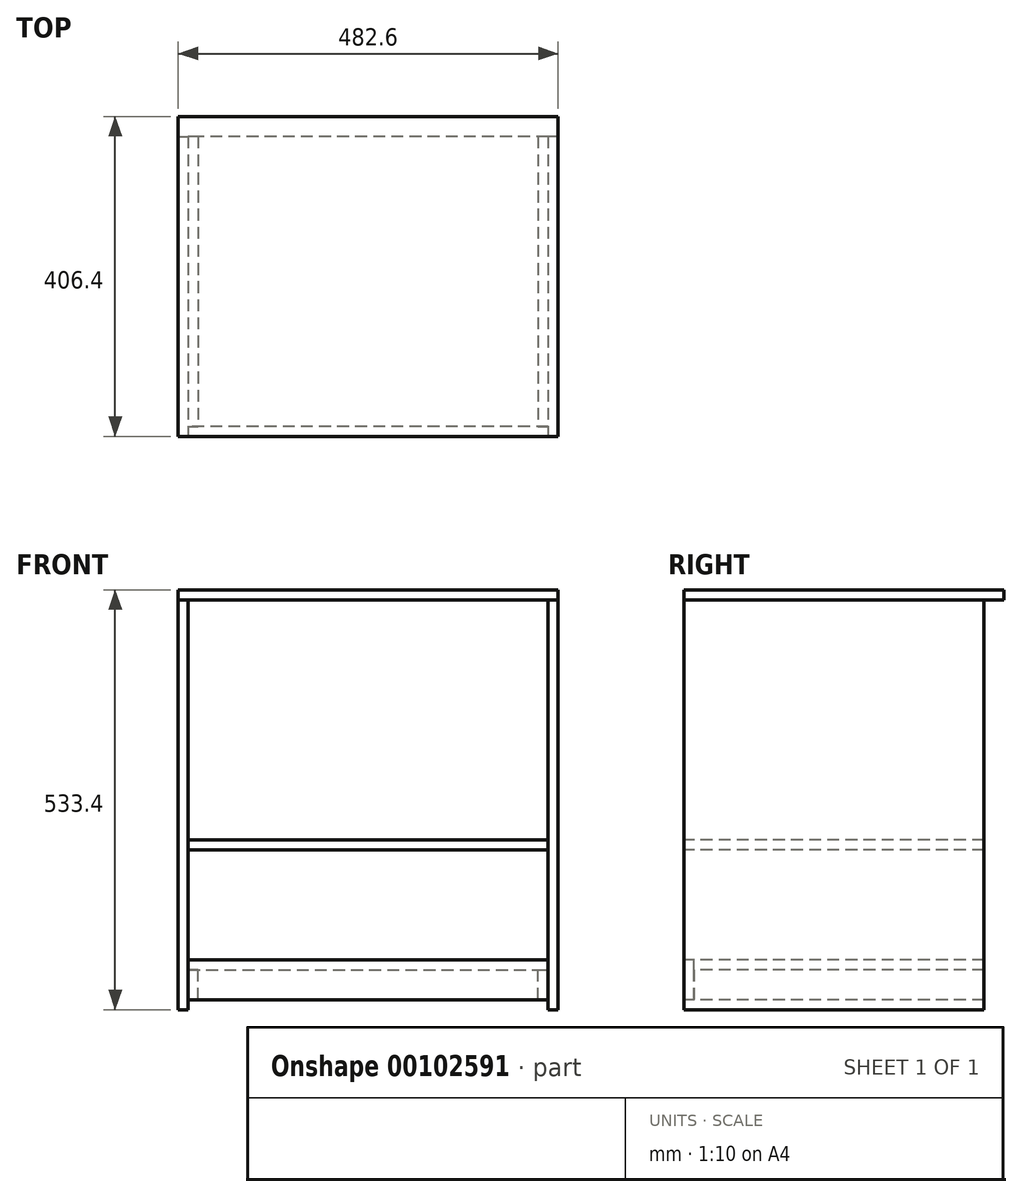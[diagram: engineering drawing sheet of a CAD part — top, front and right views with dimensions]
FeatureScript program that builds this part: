
annotation { "Feature Type Name" : "Feature", "Feature Type Description" : "" }
export const myFeature = defineFeature(function(context is Context, id is Id, definition is map)
    precondition{}
    {
        {
            var Q0;
            Q0=qCreatedBy(makeId("Front.planeOp"),FACE);
            var sketch = newSketch(context, id + "F0", { "sketchPlane" : qUnion([Q0])});
            skLineSegment(sketch, "E0.bottom", {"start": v(-241.3, 6.35) * mm, "end": v(241.3, 6.35) * mm});
            skLineSegment(sketch, "E0.top", {"start": v(-241.3, -6.35) * mm, "end": v(241.3, -6.35) * mm});
            skLineSegment(sketch, "E0.left", {"start": v(-241.3, 6.35) * mm, "end": v(-241.3, -6.35) * mm});
            skLineSegment(sketch, "E0.right", {"start": v(241.3, 6.35) * mm, "end": v(241.3, -6.35) * mm});
            skPoint(sketch, "E0.middle", {"position": v(0, 0) * mm});
            skLineSegment(sketch, "E1", {"start": v(0, 0) * mm, "end": v(0, -514.35) * mm, "construction": true});
            skLineSegment(sketch, "E2", {"start": v(-241.3, -6.35) * mm, "end": v(-241.3, -527.05) * mm});
            skLineSegment(sketch, "E3", {"start": v(-241.3, -527.05) * mm, "end": v(-228.6, -527.05) * mm});
            skLineSegment(sketch, "E4", {"start": v(-228.6, -527.05) * mm, "end": v(-228.6, -6.35) * mm});
            skLineSegment(sketch, "E5", {"start": v(-228.6, -476.25) * mm, "end": v(-215.9, -476.25) * mm});
            skLineSegment(sketch, "E6", {"start": v(-215.9, -476.25) * mm, "end": v(-215.9, -514.35) * mm});
            skLineSegment(sketch, "E7", {"start": v(-215.9, -514.35) * mm, "end": v(-228.6, -514.35) * mm});
            skLineSegment(sketch, "E8.MirrorCS", {"start": v(241.3, -527.05) * mm, "end": v(228.6, -527.05) * mm});
            skLineSegment(sketch, "E9.MirrorCS", {"start": v(228.6, -527.05) * mm, "end": v(228.6, -6.35) * mm});
            skLineSegment(sketch, "E10.MirrorCS", {"start": v(228.6, -476.25) * mm, "end": v(215.9, -476.25) * mm});
            skLineSegment(sketch, "E11.MirrorCS", {"start": v(215.9, -476.25) * mm, "end": v(215.9, -514.35) * mm});
            skLineSegment(sketch, "E12.MirrorCS", {"start": v(215.9, -514.35) * mm, "end": v(228.6, -514.35) * mm});
            skLineSegment(sketch, "E13.MirrorCS", {"start": v(241.3, -6.35) * mm, "end": v(241.3, -527.05) * mm});
            skLineSegment(sketch, "E14", {"start": v(-228.6, -463.55) * mm, "end": v(228.6, -463.55) * mm});
            skLineSegment(sketch, "E15", {"start": v(215.9, -476.25) * mm, "end": v(-215.9, -476.25) * mm});
            skLineSegment(sketch, "E16", {"start": v(-215.9, -514.35) * mm, "end": v(215.9, -514.35) * mm});
            skLineSegment(sketch, "E17", {"start": v(-228.6, -323.85) * mm, "end": v(228.6, -323.85) * mm});
            skLineSegment(sketch, "E18", {"start": v(-228.6, -311.15) * mm, "end": v(228.6, -311.15) * mm});
            skSolve(sketch);
        }
        {
            var Q0;
            Q0=makeQuery(id+"F0.imprint","IMPRINT",FACE,{"disambiguationData":[TD([[makeQuery(id+"F0.imprint","IMPRINT",EDGE,{"derivedFrom":sQuery(id+"F0.wireOp",EDGE,"E0.bottom")}),-1.0]])]});
            extrude(context, id + "F1", {"entities" : qUnion([Q0]), "oppositeDirection" : true, "depth" : 406.4 * mm});
        }
        {
            var Q0;
            {var subQ3=sQuery(id+"F0.wireOp",EDGE,"E2");Q0=makeQuery(id+"F0.imprint","IMPRINT",FACE,{"disambiguationData":[TD([[makeQuery(id+"F0.imprint","IMPRINT",EDGE,{"derivedFrom":subQ3}),1.0]])]});}
            var Q1;
            {var subQ0=sQuery(id+"F0.wireOp",EDGE,"E8.MirrorCS");Q1=makeQuery(id+"F0.imprint","IMPRINT",FACE,{"disambiguationData":[TD([[makeQuery(id+"F0.imprint","IMPRINT",EDGE,{"derivedFrom":subQ0}),-1.0]])]});}
            var Q2;
            Q2=makeQuery(id+"F1.opExtrude","CAP_FACE",FACE,{"disambiguationData":[OSD([sQuery(id+"F0.wireOp",EDGE,"E0.bottom"),sQuery(id+"F0.wireOp",EDGE,"E0.top"),sQuery(id+"F0.wireOp",EDGE,"E0.left"),sQuery(id+"F0.wireOp",EDGE,"E0.right")])],"isStart":false});
            extrude(context, id + "F2", {"entities" : qUnion([Q0, Q1]), "oppositeDirection" : true, "endBoundEntityFace" : qUnion([Q2]), "depth" : 381 * mm});
        }
        {
            var Q0;
            {var subQ3=sQuery(id+"F0.wireOp",EDGE,"E5");Q0=makeQuery(id+"F0.imprint","IMPRINT",FACE,{"disambiguationData":[TD([[makeQuery(id+"F0.imprint","IMPRINT",EDGE,{"derivedFrom":subQ3}),1.0]])]});}
            var Q1;
            Q1=makeQuery(id+"F2.opExtrude","CAP_FACE",FACE,{"disambiguationData":[OSD([sQuery(id+"F0.wireOp",EDGE,"E0.top"),sQuery(id+"F0.wireOp",EDGE,"E8.MirrorCS"),sQuery(id+"F0.wireOp",EDGE,"E9.MirrorCS"),sQuery(id+"F0.wireOp",EDGE,"E13.MirrorCS")])],"isStart":false});
            extrude(context, id + "F3", {"entities" : qUnion([Q0]), "endBound" : BoundingType.UP_TO_SURFACE, "oppositeDirection" : true, "endBoundEntityFace" : qUnion([Q1]), "depth" : 25.4 * mm, "hasSecondDirection" : true, "secondDirectionOppositeDirection" : true, "secondDirectionDepth" : 12.7 * mm});
        }
        {
            var Q0;
            {var subQ0=sQuery(id+"F0.wireOp",EDGE,"E5");Q0=makeQuery(id+"F0.imprint","IMPRINT",FACE,{"disambiguationData":[TD([[makeQuery(id+"F0.imprint","IMPRINT",EDGE,{"derivedFrom":subQ0}),-1.0]])]});}
            var Q1;
            {var subQ0=sQuery(id+"F0.wireOp",EDGE,"E10.MirrorCS");Q1=makeQuery(id+"F0.imprint","IMPRINT",FACE,{"disambiguationData":[TD([[makeQuery(id+"F0.imprint","IMPRINT",EDGE,{"derivedFrom":subQ0}),1.0]])]});}
            var Q2;
            Q2=makeQuery(id+"F3.opExtrude","CAP_FACE",FACE,{"disambiguationData":[OSD([sQuery(id+"F0.wireOp",EDGE,"E4"),sQuery(id+"F0.wireOp",EDGE,"E5"),sQuery(id+"F0.wireOp",EDGE,"E9.MirrorCS"),sQuery(id+"F0.wireOp",EDGE,"E10.MirrorCS"),sQuery(id+"F0.wireOp",EDGE,"E14"),sQuery(id+"F0.wireOp",EDGE,"E15")])],"isStart":false});
            var Q3;
            Q3=makeQuery(id+"F3.opExtrude","CAP_FACE",FACE,{"disambiguationData":[OSD([sQuery(id+"F0.wireOp",EDGE,"E4"),sQuery(id+"F0.wireOp",EDGE,"E5"),sQuery(id+"F0.wireOp",EDGE,"E9.MirrorCS"),sQuery(id+"F0.wireOp",EDGE,"E10.MirrorCS"),sQuery(id+"F0.wireOp",EDGE,"E14"),sQuery(id+"F0.wireOp",EDGE,"E15")])],"isStart":true});
            extrude(context, id + "F4", {"entities" : qUnion([Q0, Q1]), "endBound" : BoundingType.UP_TO_SURFACE, "oppositeDirection" : true, "endBoundEntityFace" : qUnion([Q2]), "depth" : 25.4 * mm, "hasSecondDirection" : true, "secondDirectionOppositeDirection" : true, "secondDirectionBoundEntityFace" : qUnion([Q3]), "secondDirectionDepth" : 12.7 * mm});
        }
        {
            var Q0;
            {var subQ0=sQuery(id+"F0.wireOp",EDGE,"E5");Q0=makeQuery(id+"F0.imprint","IMPRINT",FACE,{"disambiguationData":[TD([[makeQuery(id+"F0.imprint","IMPRINT",EDGE,{"derivedFrom":subQ0}),-1.0]])]});}
            var Q1;
            Q1=makeQuery(id+"F0.imprint","IMPRINT",FACE,{"disambiguationData":[TD([[makeQuery(id+"F0.imprint","IMPRINT",EDGE,{"derivedFrom":sQuery(id+"F0.wireOp",EDGE,"E6")}),1.0]])]});
            var Q2;
            {var subQ3=sQuery(id+"F0.wireOp",EDGE,"E5");Q2=makeQuery(id+"F0.imprint","IMPRINT",FACE,{"disambiguationData":[TD([[makeQuery(id+"F0.imprint","IMPRINT",EDGE,{"derivedFrom":subQ3}),1.0]])]});}
            var Q3;
            {var subQ0=sQuery(id+"F0.wireOp",EDGE,"E10.MirrorCS");Q3=makeQuery(id+"F0.imprint","IMPRINT",FACE,{"disambiguationData":[TD([[makeQuery(id+"F0.imprint","IMPRINT",EDGE,{"derivedFrom":subQ0}),1.0]])]});}
            extrude(context, id + "F5", {"entities" : qUnion([Q0, Q1, Q2, Q3]), "oppositeDirection" : true, "depth" : 12.7 * mm});
        }
        {
            var Q0;
            {var subQ0=sQuery(id+"F0.wireOp",EDGE,"E17");Q0=makeQuery(id+"F0.imprint","IMPRINT",FACE,{"disambiguationData":[TD([[makeQuery(id+"F0.imprint","IMPRINT",EDGE,{"derivedFrom":subQ0}),1.0]])]});}
            var Q1;
            Q1=makeQuery(id+"F3.opExtrude","CAP_FACE",FACE,{"disambiguationData":[OSD([sQuery(id+"F0.wireOp",EDGE,"E4"),sQuery(id+"F0.wireOp",EDGE,"E5"),sQuery(id+"F0.wireOp",EDGE,"E9.MirrorCS"),sQuery(id+"F0.wireOp",EDGE,"E10.MirrorCS"),sQuery(id+"F0.wireOp",EDGE,"E14"),sQuery(id+"F0.wireOp",EDGE,"E15")])],"isStart":false});
            extrude(context, id + "F6", {"entities" : qUnion([Q0]), "endBound" : BoundingType.UP_TO_SURFACE, "oppositeDirection" : true, "endBoundEntityFace" : qUnion([Q1]), "depth" : 25.4 * mm});
        }
    });
